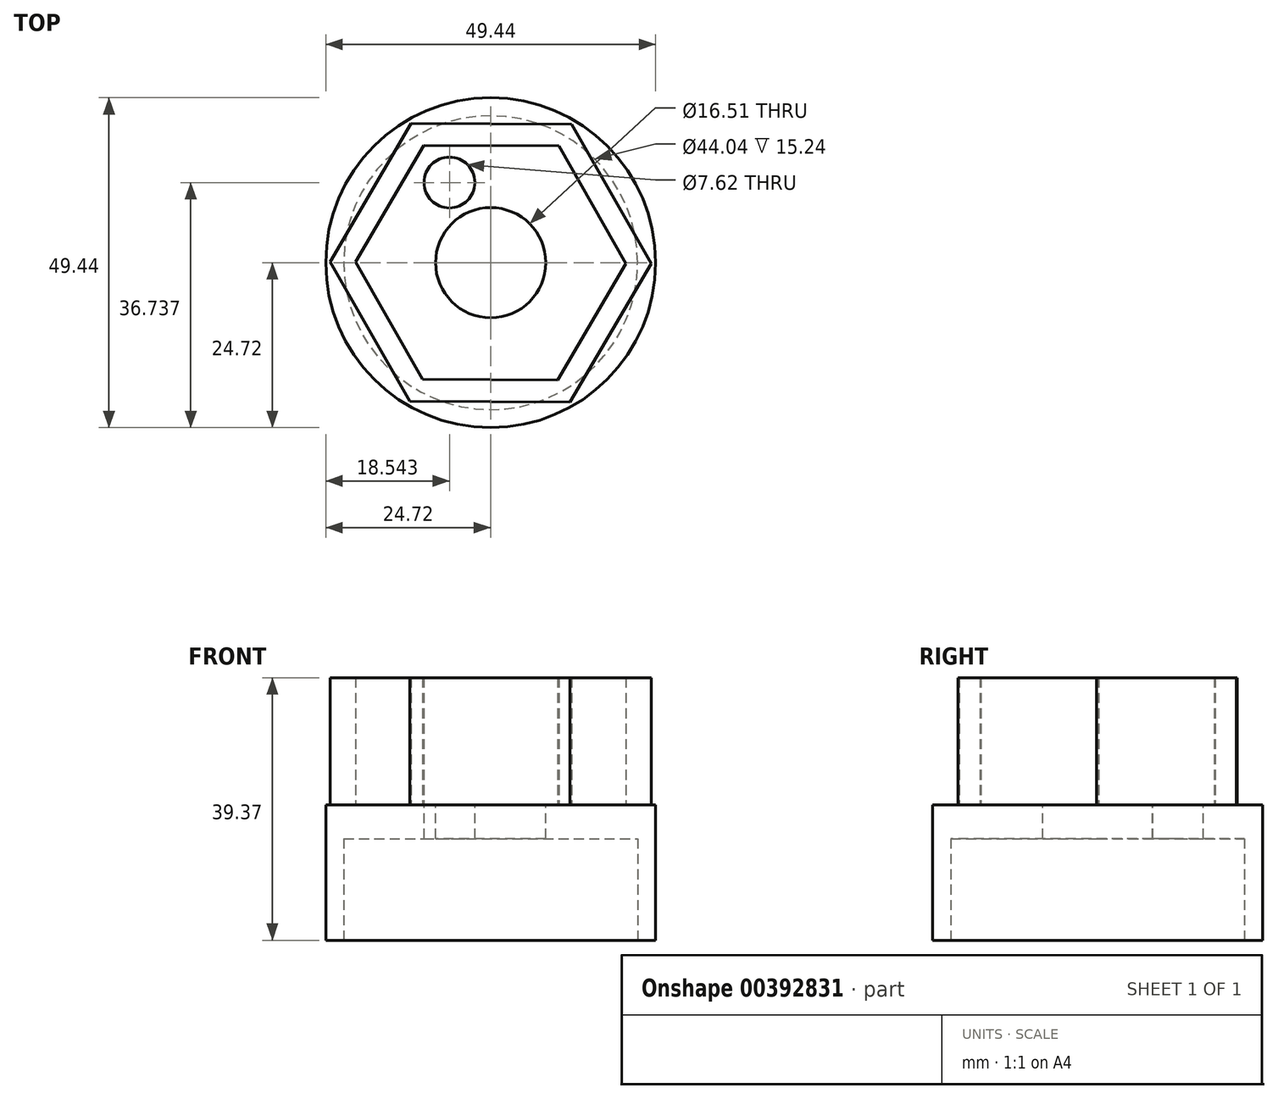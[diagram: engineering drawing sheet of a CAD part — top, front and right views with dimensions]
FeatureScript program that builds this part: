
annotation { "Feature Type Name" : "Feature", "Feature Type Description" : "" }
export const myFeature = defineFeature(function(context is Context, id is Id, definition is map)
    precondition{}
    {
        {
            var Q0;
            Q0=qCreatedBy(makeId("Top.planeOp"),FACE);
            var sketch = newSketch(context, id + "F0", { "sketchPlane" : qUnion([Q0])});
            skCircle(sketch, "E0.cCircle", {"center": v(0, 0) * mm, "radius": 20.83 * mm, "construction": true});
            skLineSegment(sketch, "E0.0", {"start": v(24.05, -0.13) * mm, "end": v(11.91, -20.9) * mm});
            skLineSegment(sketch, "E0.1", {"start": v(11.91, -20.9) * mm, "end": v(-12.14, -20.77) * mm});
            skLineSegment(sketch, "E0.2", {"start": v(-12.14, -20.77) * mm, "end": v(-24.05, 0.13) * mm});
            skLineSegment(sketch, "E0.3", {"start": v(-24.05, 0.13) * mm, "end": v(-11.91, 20.9) * mm});
            skLineSegment(sketch, "E0.4", {"start": v(-11.91, 20.9) * mm, "end": v(12.14, 20.77) * mm});
            skLineSegment(sketch, "E0.5", {"start": v(12.14, 20.77) * mm, "end": v(24.05, -0.13) * mm});
            skPoint(sketch, "E0.0.midPoint", {"position": v(17.98, -10.52) * mm});
            skSolve(sketch);
        }
        {
            var Q0;
            Q0=makeQuery(id+"F0.imprint","IMPRINT",FACE,{"disambiguationData":[TD([[makeQuery(id+"F0.imprint","IMPRINT",EDGE,{"derivedFrom":sQuery(id+"F0.wireOp",EDGE,"E0.0")}),-1.0]])]});
            var sketch = newSketch(context, id + "F1", { "sketchPlane" : qUnion([Q0])});
            skCircle(sketch, "E1.cCircle", {"center": v(0, 0) * mm, "radius": 17.54 * mm, "construction": true});
            skLineSegment(sketch, "E1.0", {"start": v(10.22, 17.49) * mm, "end": v(20.26, -0.11) * mm});
            skLineSegment(sketch, "E1.1", {"start": v(20.26, -0.11) * mm, "end": v(10.03, -17.6) * mm});
            skLineSegment(sketch, "E1.2", {"start": v(10.03, -17.6) * mm, "end": v(-10.22, -17.49) * mm});
            skLineSegment(sketch, "E1.3", {"start": v(-10.22, -17.49) * mm, "end": v(-20.26, 0.11) * mm});
            skLineSegment(sketch, "E1.4", {"start": v(-20.26, 0.11) * mm, "end": v(-10.03, 17.6) * mm});
            skLineSegment(sketch, "E1.5", {"start": v(-10.03, 17.6) * mm, "end": v(10.22, 17.49) * mm});
            skPoint(sketch, "E1.0.midPoint", {"position": v(15.24, 8.69) * mm});
            skSolve(sketch);
        }
        {
            var Q0;
            Q0=qSketchRegion(id+"F0",true);
            extrude(context, id + "F2", {"entities" : qUnion([Q0]), "depth" : 19.05 * mm});
        }
        {
            var Q0;
            Q0=makeQuery(id+"F1.imprint","IMPRINT",FACE,{"disambiguationData":[TD([[makeQuery(id+"F1.imprint","IMPRINT",EDGE,{"derivedFrom":sQuery(id+"F1.wireOp",EDGE,"E1.0")}),-1.0]])]});
            extrude(context, id + "F3", {"entities" : qUnion([Q0]), "operationType" : NewBodyOperationType.REMOVE, "depth" : 67.82 * mm});
        }
        {
            var Q0;
            Q0=qCreatedBy(makeId("Top.planeOp"),FACE);
            var sketch = newSketch(context, id + "F4", { "sketchPlane" : qUnion([Q0])});
            skCircle(sketch, "E2", {"center": v(0, 0) * mm, "radius": 24.72 * mm});
            skSolve(sketch);
        }
        {
            var Q0;
            Q0=makeQuery(id+"F4.imprint","IMPRINT",FACE,{"disambiguationData":[TD([[makeQuery(id+"F4.imprint","IMPRINT",EDGE,{"derivedFrom":sQuery(id+"F4.wireOp",EDGE,"E2")}),1.0]])]});
            extrude(context, id + "F5", {"entities" : qUnion([Q0]), "operationType" : NewBodyOperationType.ADD, "oppositeDirection" : true, "depth" : 2.54 * mm});
        }
        {
            var Q0;
            Q0=makeQuery(id+"F5.boolean.opBoolean","SPLIT",FACE,{"disambiguationData":[TD([makeQuery(id+"F3.boolean.opBoolean","COPY",FACE,{"derivedFrom":makeQuery(id+"F3.opExtrude","SWEPT_FACE",FACE,{"disambiguationData":[OSD([sQuery(id+"F1.wireOp",EDGE,"E1.0")])]})})])],"derivedFrom":makeQuery(id+"F5.opExtrude","CAP_FACE",FACE,{"disambiguationData":[OSD([sQuery(id+"F4.wireOp",EDGE,"E2")])],"isStart":true})});
            var sketch = newSketch(context, id + "F6", { "sketchPlane" : qUnion([Q0])});
            skCircle(sketch, "E3", {"center": v(0, 0) * mm, "radius": 8.26 * mm});
            skSolve(sketch);
        }
        {
            var Q0;
            Q0=makeQuery(id+"F6.imprint","IMPRINT",FACE,{"disambiguationData":[TD([[makeQuery(id+"F6.imprint","IMPRINT",EDGE,{"derivedFrom":sQuery(id+"F6.wireOp",EDGE,"E3")}),1.0]])]});
            extrude(context, id + "F7", {"entities" : qUnion([Q0]), "operationType" : NewBodyOperationType.REMOVE, "oppositeDirection" : true, "depth" : 60.7 * mm});
        }
        {
            var Q0;
            Q0=makeQuery(id+"F5.opExtrude","CAP_FACE",FACE,{"disambiguationData":[OSD([sQuery(id+"F4.wireOp",EDGE,"E2")])],"isStart":false});
            extrude(context, id + "F8", {"entities" : qUnion([Q0]), "operationType" : NewBodyOperationType.ADD, "depth" : 17.78 * mm});
        }
        {
            var Q0;
            Q0=makeQuery(id+"F8.opExtrude","CAP_FACE",FACE,{"disambiguationData":[OSD([sQuery(id+"F4.wireOp",EDGE,"E2")])],"isStart":false});
            var sketch = newSketch(context, id + "F9", { "sketchPlane" : qUnion([Q0])});
            skCircle(sketch, "E4", {"center": v(0, 0) * mm, "radius": 22.02 * mm});
            skSolve(sketch);
        }
        {
            var Q0;
            Q0=makeQuery(id+"F9.imprint","IMPRINT",FACE,{"disambiguationData":[TD([[makeQuery(id+"F9.imprint","IMPRINT",EDGE,{"derivedFrom":sQuery(id+"F9.wireOp",EDGE,"E4")}),1.0]])]});
            extrude(context, id + "F10", {"entities" : qUnion([Q0]), "operationType" : NewBodyOperationType.REMOVE, "oppositeDirection" : true, "depth" : 15.24 * mm});
        }
        {
            var Q0;
            Q0=makeQuery(id+"F5.boolean.opBoolean","SPLIT",FACE,{"disambiguationData":[TD([makeQuery(id+"F3.boolean.opBoolean","COPY",FACE,{"derivedFrom":makeQuery(id+"F3.opExtrude","SWEPT_FACE",FACE,{"disambiguationData":[OSD([sQuery(id+"F1.wireOp",EDGE,"E1.0")])]})})])],"derivedFrom":makeQuery(id+"F5.opExtrude","CAP_FACE",FACE,{"disambiguationData":[OSD([sQuery(id+"F4.wireOp",EDGE,"E2")])],"isStart":true})});
            var sketch = newSketch(context, id + "F11", { "sketchPlane" : qUnion([Q0])});
            skCircle(sketch, "E5", {"center": v(-6.18, 12.02) * mm, "radius": 3.8 * mm});
            skSolve(sketch);
        }
        {
            var Q0;
            Q0=makeQuery(id+"F11.imprint","IMPRINT",FACE,{"disambiguationData":[TD([[makeQuery(id+"F11.imprint","IMPRINT",EDGE,{"derivedFrom":sQuery(id+"F11.wireOp",EDGE,"E5")}),1.0]])]});
            extrude(context, id + "F12", {"entities" : qUnion([Q0]), "operationType" : NewBodyOperationType.REMOVE, "oppositeDirection" : true, "depth" : 25.4 * mm});
        }
    });
